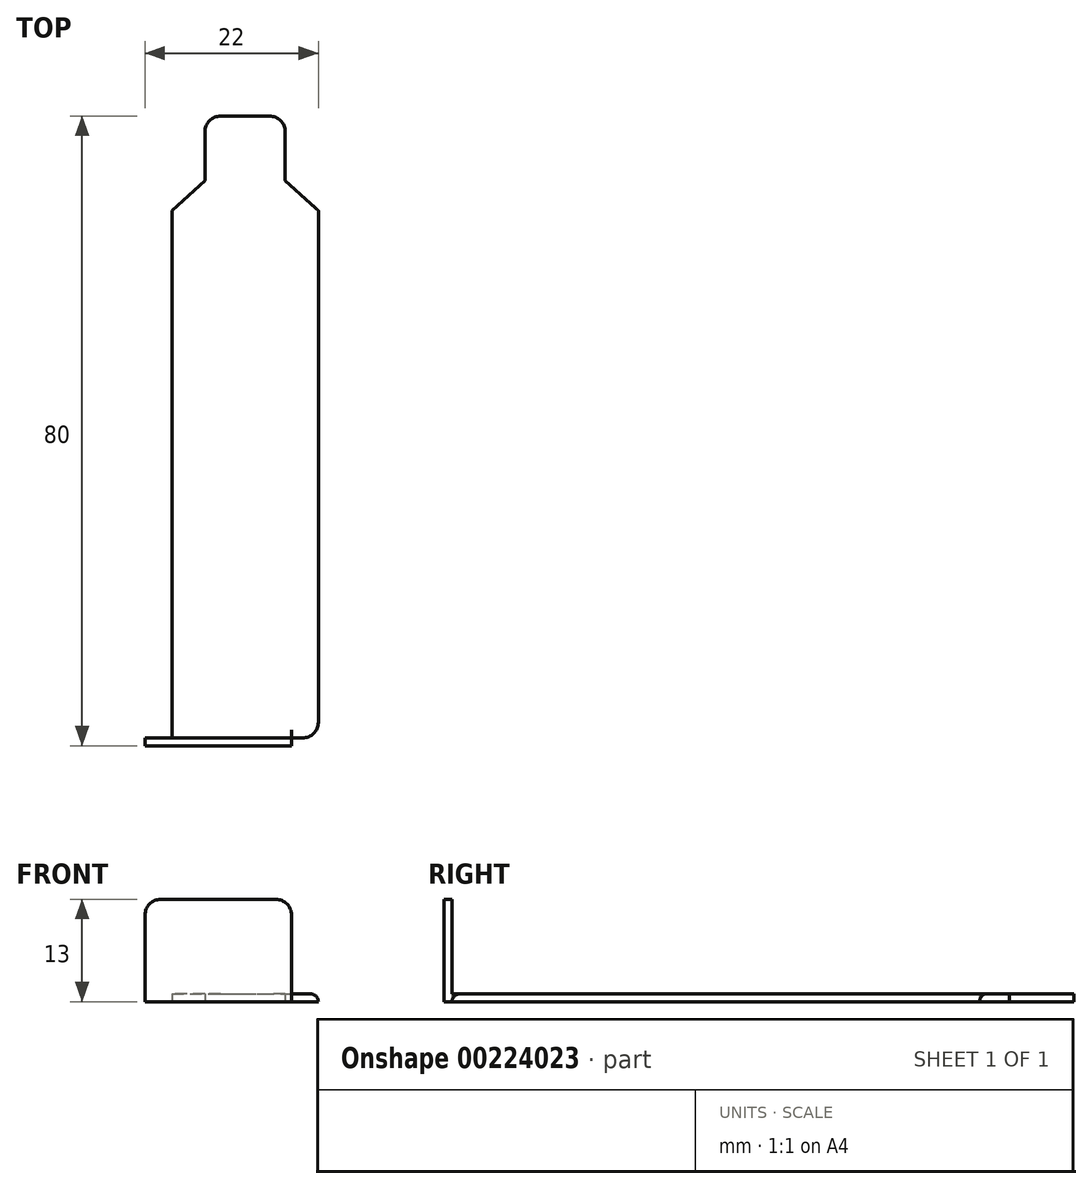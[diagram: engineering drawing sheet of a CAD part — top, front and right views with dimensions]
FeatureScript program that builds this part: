
annotation { "Feature Type Name" : "Feature", "Feature Type Description" : "" }
export const myFeature = defineFeature(function(context is Context, id is Id, definition is map)
    precondition{}
    {
        {
            var Q0;
            Q0=qCreatedBy(makeId("Top.planeOp"),FACE);
            var sketch = newSketch(context, id + "F0", { "sketchPlane" : qUnion([Q0])});
            skLineSegment(sketch, "E0.bottom", {"start": v(0, 0) * mm, "end": v(18.6, 0) * mm});
            skLineSegment(sketch, "E0.top", {"start": v(4.2, 79) * mm, "end": v(14.4, 79) * mm});
            skLineSegment(sketch, "E0.left", {"start": v(0, 0) * mm, "end": v(0, 67) * mm});
            skLineSegment(sketch, "E0.right", {"start": v(18.6, 0) * mm, "end": v(18.6, 67) * mm});
            skLineSegment(sketch, "E1", {"start": v(4.2, 79) * mm, "end": v(4.2, 70.8) * mm});
            skLineSegment(sketch, "E2", {"start": v(4.2, 70.8) * mm, "end": v(0, 67) * mm});
            skLineSegment(sketch, "E3", {"start": v(9.3, 79) * mm, "end": v(9.3, 0) * mm, "construction": true});
            skLineSegment(sketch, "E4.MirrorCS", {"start": v(14.4, 79) * mm, "end": v(14.4, 70.8) * mm});
            skLineSegment(sketch, "E5.MirrorCS", {"start": v(14.4, 70.8) * mm, "end": v(18.6, 67) * mm});
            skPoint(sketch, "E6.visualSharp", {"position": v(4.2, 79) * mm});
            skPoint(sketch, "E7.visualSharp", {"position": v(14.4, 79) * mm});
            skSolve(sketch);
        }
        {
            var Q0;
            Q0=qSketchRegion(id+"F0",true);
            extrude(context, id + "F1", {"entities" : qUnion([Q0]), "depth" : 1 * mm});
        }
        {
            var Q0;
            Q0=qCreatedBy(makeId("Top.planeOp"),FACE);
            var sketch = newSketch(context, id + "F2", { "sketchPlane" : qUnion([Q0])});
            skLineSegment(sketch, "E8.bottom", {"start": v(15.2, 0) * mm, "end": v(-3.4, 0) * mm});
            skLineSegment(sketch, "E9.top", {"start": v(15.2, -1) * mm, "end": v(-3.4, -1) * mm});
            skLineSegment(sketch, "E9.left", {"start": v(15.2, 0) * mm, "end": v(15.2, -1) * mm});
            skLineSegment(sketch, "E9.right", {"start": v(-3.4, 0) * mm, "end": v(-3.4, -1) * mm});
            skSolve(sketch);
        }
        {
            var Q0;
            Q0=qSketchRegion(id+"F2",true);
            extrude(context, id + "F3", {"entities" : qUnion([Q0]), "operationType" : NewBodyOperationType.ADD, "depth" : 13 * mm});
        }
        {
            var Q0;
            Q0=makeQuery(id+"F1.opExtrude","SWEPT_EDGE",EDGE,{"disambiguationData":[OSD([sQuery(id+"F0.wireOp",EDGE,"E0.bottom"),sQuery(id+"F0.wireOp",EDGE,"E0.right")])]});
            var Q1;
            Q1=makeQuery(id+"F3.opExtrude","CAP_EDGE",EDGE,{"disambiguationData":[OSD([sQuery(id+"F2.wireOp",EDGE,"E9.left")])],"isStart":false});
            var Q2;
            Q2=makeQuery(id+"F3.opExtrude","CAP_EDGE",EDGE,{"disambiguationData":[OSD([sQuery(id+"F2.wireOp",EDGE,"E9.right")])],"isStart":false});
            var Q3;
            Q3=makeQuery(id+"F1.opExtrude","SWEPT_EDGE",EDGE,{"disambiguationData":[OSD([sQuery(id+"F0.wireOp",EDGE,"E0.top"),sQuery(id+"F0.wireOp",EDGE,"E4.MirrorCS")])]});
            var Q4;
            Q4=makeQuery(id+"F1.opExtrude","SWEPT_EDGE",EDGE,{"disambiguationData":[OSD([sQuery(id+"F0.wireOp",EDGE,"E0.top"),sQuery(id+"F0.wireOp",EDGE,"E1")])]});
            fillet(context, id + "F4", {"entities" : qUnion([Q0, Q1, Q2, Q3, Q4]), "radius" : 2 * mm, "tangentPropagation" : true, "allowEdgeOverflow" : false});
        }
        {
            var Q0;
            {var subQ0=sQuery(id+"F0.wireOp",EDGE,"E0.left");var subQ1=sQuery(id+"F0.wireOp",EDGE,"E0.bottom");Q0=makeQuery(id+"F3.boolean.opBoolean","SPLIT",EDGE,{"disambiguationData":[TD([makeQuery(id+"F1.opExtrude","SWEPT_FACE",FACE,{"disambiguationData":[OSD([subQ0])]})])],"derivedFrom":makeQuery(id+"F1.opExtrude","CAP_EDGE",EDGE,{"disambiguationData":[OSD([subQ1])],"isStart":false})});}
            fillet(context, id + "F5", {"entities" : qUnion([Q0]), "radius" : 1 * mm, "tangentPropagation" : true, "allowEdgeOverflow" : false});
        }
    });
